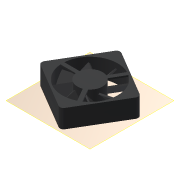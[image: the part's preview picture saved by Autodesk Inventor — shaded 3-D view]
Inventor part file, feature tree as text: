
AUTODESK INVENTOR PART (.ipt)
format: ipt  version: 2016 (Build 200138000, 138)  size: 203,264 bytes
history: native  units: mm
features: extrude x5, sketch x5, reference x4, pattern_circular x2, plane x1, projected_geometry x1
ambient origin geometry x8: Origin, YZ Plane, XZ Plane, XY Plane, X Axis, Y Axis, Z Axis, Center Point
bodies: Solid1 (feature_tree), Solid2 (feature_tree)
feature tree (18):
  plane  "Work Plane1"
  extrude  "Extrusion1"  Depth=5.0mm
  extrude  "Extrusion2"  Depth=25.0mm
  extrude  "Extrusion3"  Depth=25.0mm TaperAngle=0.0deg
  pattern_circular  "Circular Pattern1"  Count=3 Angle=360.0deg
  extrude  "Extrusion4"  Depth=2.0mm TaperAngle=0.0deg
  pattern_circular  "Circular Pattern2"  Count=8 Angle=360.0deg
  extrude  "Extrusion5"  Depth=80.0mm TaperAngle=0.0deg
  sketch  "Sketch1"  dims[d0=80.0mm d1=5.0mm]
  reference  "Reference1"
  reference  "Reference2"
  reference  "Reference3"
  reference  "Reference4"
  sketch  "Sketch2"  dims[d2=25.0mm d3=0.0mm d4=34.0mm]
  projected_geometry  "Projected Loop1"
  sketch  "Sketch3"  dims[d5=75.0mm d6=25.0mm d7=0.0mm]
  sketch  "Sketch4"  dims[d8=2.0mm d9=0.0mm d10=30.0mm d11=360.0deg]
  sketch  "Sketch5"  dims[d13=8.726646mm d14=2.0mm d15=0.0mm d16=80.0mm d17=360.0deg d19=40.0mm d20=0.0mm]
